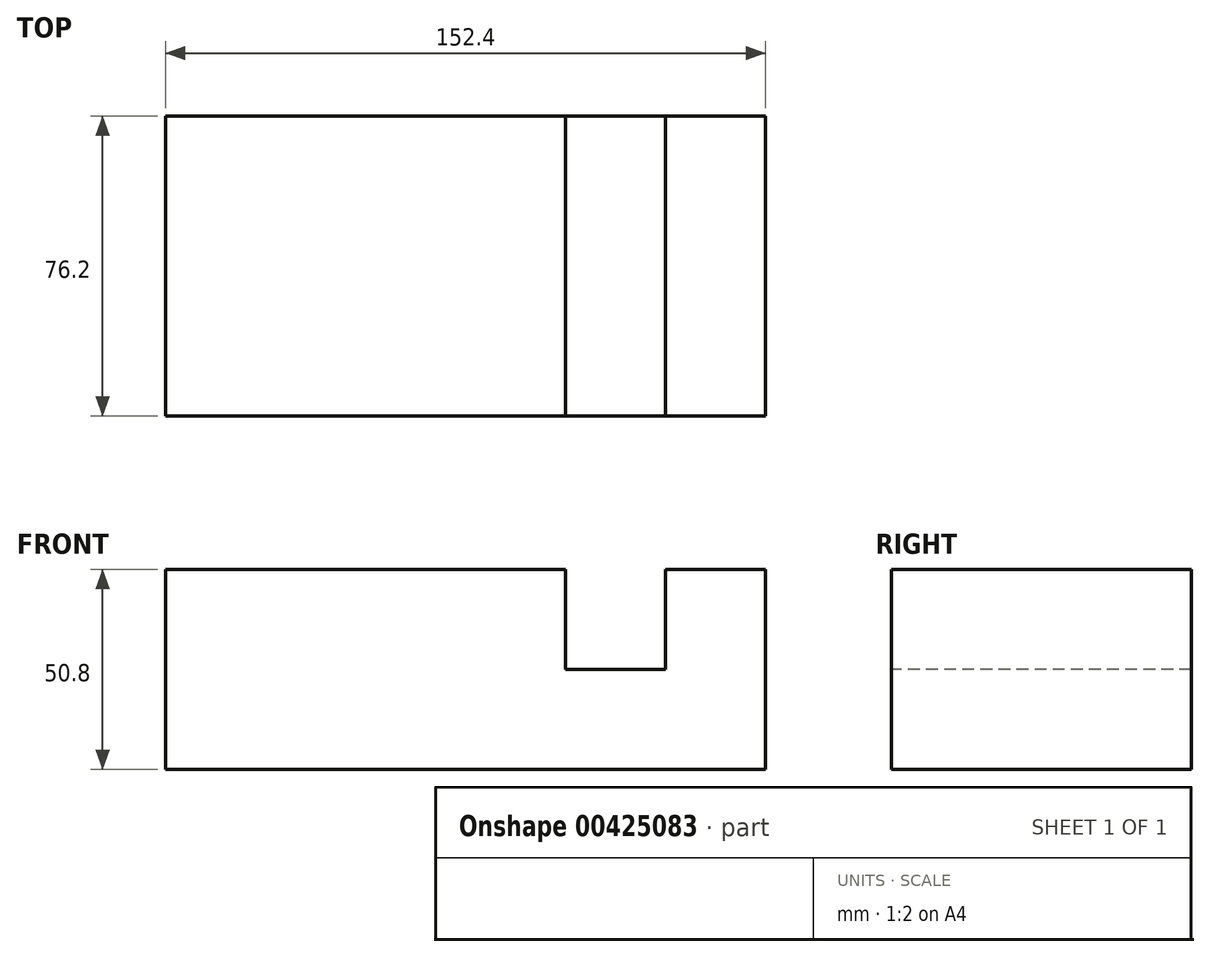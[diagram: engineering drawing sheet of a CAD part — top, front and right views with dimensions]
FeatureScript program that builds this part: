
annotation { "Feature Type Name" : "Feature", "Feature Type Description" : "" }
export const myFeature = defineFeature(function(context is Context, id is Id, definition is map)
    precondition{}
    {
        {
            var Q0;
            Q0=qCreatedBy(makeId("Front.planeOp"),FACE);
            var sketch = newSketch(context, id + "F0", { "sketchPlane" : qUnion([Q0])});
            skLineSegment(sketch, "E0", {"start": v(0, 0) * mm, "end": v(152.4, 0) * mm});
            skLineSegment(sketch, "E1", {"start": v(152.4, 0) * mm, "end": v(152.4, 50.8) * mm});
            skLineSegment(sketch, "E2", {"start": v(152.4, 50.8) * mm, "end": v(0, 50.8) * mm});
            skLineSegment(sketch, "E3", {"start": v(0, 50.8) * mm, "end": v(0, 0) * mm});
            skSolve(sketch);
        }
        {
            var Q0;
            Q0=makeQuery(id+"F0.imprint","IMPRINT",FACE,{"disambiguationData":[TD([[makeQuery(id+"F0.imprint","IMPRINT",EDGE,{"derivedFrom":sQuery(id+"F0.wireOp",EDGE,"E0")}),1.0]])]});
            extrude(context, id + "F1", {"entities" : qUnion([Q0]), "depth" : 76.2 * mm});
        }
        {
            var Q0;
            Q0=makeQuery(id+"F1.opExtrude","CAP_FACE",FACE,{"disambiguationData":[OSD([sQuery(id+"F0.wireOp",EDGE,"E0"),sQuery(id+"F0.wireOp",EDGE,"E1"),sQuery(id+"F0.wireOp",EDGE,"E2"),sQuery(id+"F0.wireOp",EDGE,"E3")])],"isStart":false});
            var sketch = newSketch(context, id + "F2", { "sketchPlane" : qUnion([Q0])});
            skLineSegment(sketch, "E4", {"start": v(152.4, 50.8) * mm, "end": v(127, 50.8) * mm});
            skLineSegment(sketch, "E5", {"start": v(127, 50.8) * mm, "end": v(127, 25.4) * mm});
            skLineSegment(sketch, "E6", {"start": v(127, 25.4) * mm, "end": v(101.6, 25.4) * mm});
            skLineSegment(sketch, "E7", {"start": v(101.6, 25.4) * mm, "end": v(101.6, 50.8) * mm});
            skLineSegment(sketch, "E8", {"start": v(101.6, 50.8) * mm, "end": v(127, 50.8) * mm});
            skSolve(sketch);
        }
        {
            var Q0;
            Q0=makeQuery(id+"F2.imprint","IMPRINT",FACE,{"disambiguationData":[TD([[makeQuery(id+"F2.imprint","IMPRINT",EDGE,{"derivedFrom":sQuery(id+"F2.wireOp",EDGE,"E5")}),-1.0]])]});
            extrude(context, id + "F3", {"entities" : qUnion([Q0]), "operationType" : NewBodyOperationType.REMOVE, "oppositeDirection" : true, "depth" : 76.2 * mm});
        }
    });
